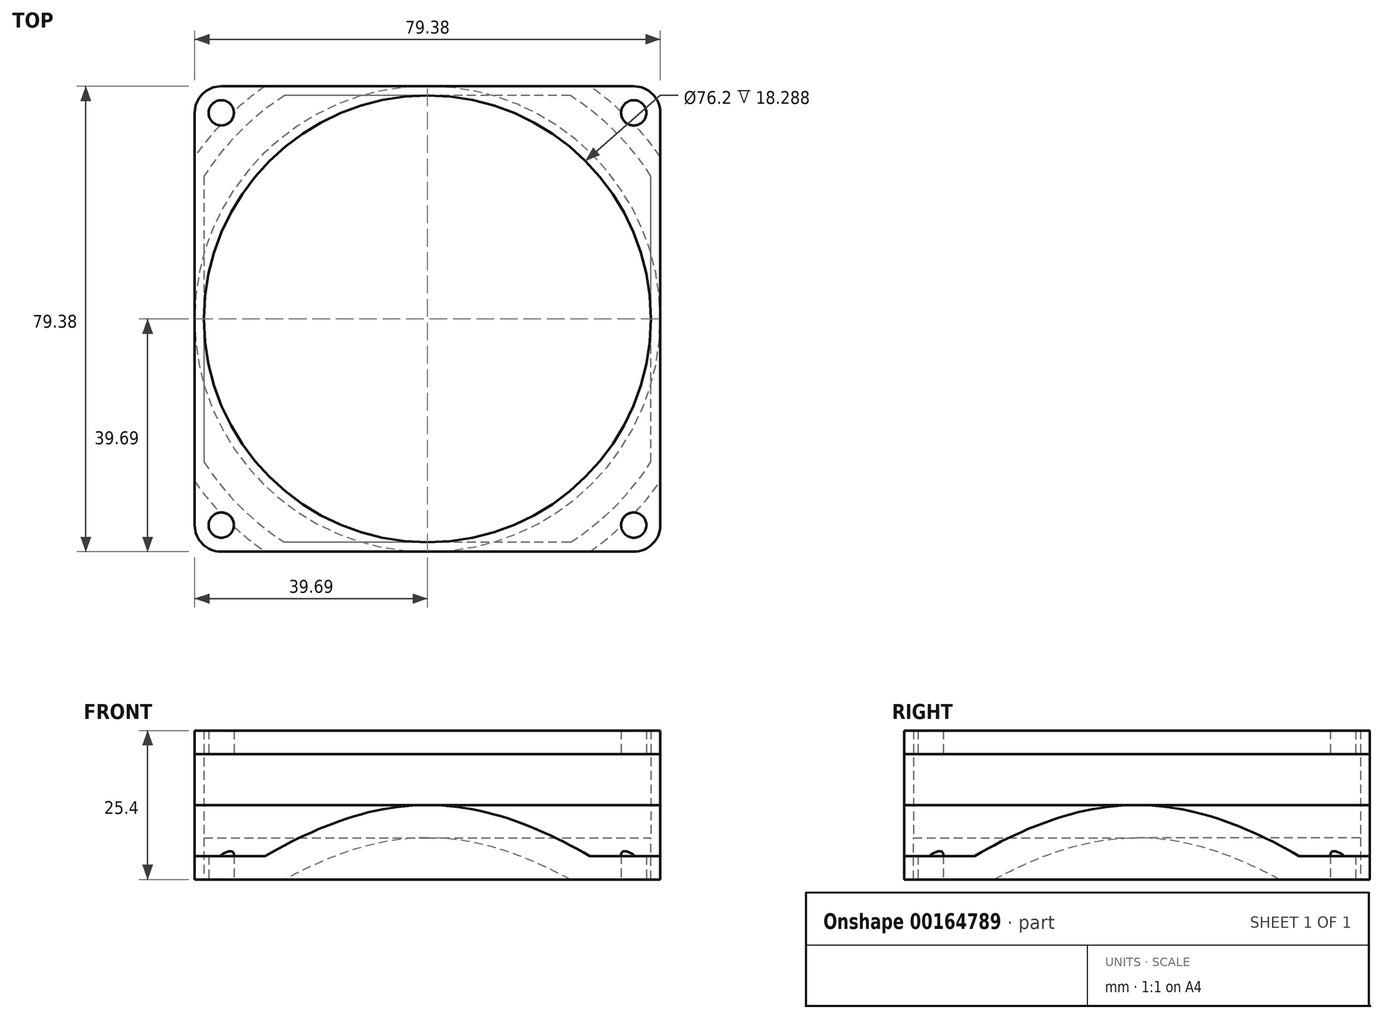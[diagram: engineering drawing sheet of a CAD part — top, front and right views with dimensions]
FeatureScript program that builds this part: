
annotation { "Feature Type Name" : "Feature", "Feature Type Description" : "" }
export const myFeature = defineFeature(function(context is Context, id is Id, definition is map)
    precondition{}
    {
        {
            var Q0;
            Q0=qCreatedBy(makeId("Top.planeOp"),FACE);
            var sketch = newSketch(context, id + "F0", { "sketchPlane" : qUnion([Q0])});
            skLineSegment(sketch, "E0.bottom", {"start": v(39.69, 39.69) * mm, "end": v(-39.69, 39.69) * mm});
            skLineSegment(sketch, "E0.top", {"start": v(39.69, -39.69) * mm, "end": v(-39.69, -39.69) * mm});
            skLineSegment(sketch, "E0.left", {"start": v(39.69, 39.69) * mm, "end": v(39.69, -39.69) * mm});
            skLineSegment(sketch, "E0.right", {"start": v(-39.69, 39.69) * mm, "end": v(-39.69, -39.69) * mm});
            skPoint(sketch, "E0.middle", {"position": v(0, 0) * mm});
            skCircle(sketch, "E1", {"center": v(0, 0) * mm, "radius": 38.1 * mm});
            skLineSegment(sketch, "E2", {"start": v(35.15, 39.69) * mm, "end": v(35.15, 35.15) * mm, "construction": true});
            skLineSegment(sketch, "E3", {"start": v(35.15, 35.15) * mm, "end": v(39.69, 35.15) * mm, "construction": true});
            skLineSegment(sketch, "E4.bottom", {"start": v(35.15, 35.15) * mm, "end": v(-35.15, 35.15) * mm, "construction": true});
            skLineSegment(sketch, "E4.top", {"start": v(35.15, -35.15) * mm, "end": v(-35.15, -35.15) * mm, "construction": true});
            skLineSegment(sketch, "E4.left", {"start": v(35.15, 35.15) * mm, "end": v(35.15, -35.15) * mm, "construction": true});
            skLineSegment(sketch, "E4.right", {"start": v(-35.15, 35.15) * mm, "end": v(-35.15, -35.15) * mm, "construction": true});
            skCircle(sketch, "E5", {"center": v(35.15, 35.15) * mm, "radius": 2.15 * mm});
            skCircle(sketch, "E6", {"center": v(-35.15, 35.15) * mm, "radius": 2.15 * mm});
            skCircle(sketch, "E7", {"center": v(-35.15, -35.15) * mm, "radius": 2.15 * mm});
            skCircle(sketch, "E8", {"center": v(35.15, -35.15) * mm, "radius": 2.15 * mm});
            skSolve(sketch);
        }
        {
            var Q0;
            Q0=qSketchRegion(id+"F0",true);
            extrude(context, id + "F1", {"entities" : qUnion([Q0]), "depth" : 25.4 * mm});
        }
        {
            var Q0;
            Q0=makeQuery(id+"F1.opExtrude","SWEPT_EDGE",EDGE,{"disambiguationData":[OSD([sQuery(id+"F0.wireOp",EDGE,"E0.bottom"),sQuery(id+"F0.wireOp",EDGE,"E0.left")])]});
            var Q1;
            Q1=makeQuery(id+"F1.opExtrude","SWEPT_EDGE",EDGE,{"disambiguationData":[OSD([sQuery(id+"F0.wireOp",EDGE,"E0.top"),sQuery(id+"F0.wireOp",EDGE,"E0.right")])]});
            var Q2;
            Q2=makeQuery(id+"F1.opExtrude","SWEPT_EDGE",EDGE,{"disambiguationData":[OSD([sQuery(id+"F0.wireOp",EDGE,"E0.top"),sQuery(id+"F0.wireOp",EDGE,"E0.left")])]});
            var Q3;
            Q3=makeQuery(id+"F1.opExtrude","SWEPT_EDGE",EDGE,{"disambiguationData":[OSD([sQuery(id+"F0.wireOp",EDGE,"E0.bottom"),sQuery(id+"F0.wireOp",EDGE,"E0.right")])]});
            fillet(context, id + "F2", {"entities" : qUnion([Q0, Q1, Q2, Q3]), "radius" : 4.53 * mm, "tangentPropagation" : true, "allowEdgeOverflow" : false});
        }
        {
            var Q0;
            Q0=qCreatedBy(makeId("Right.planeOp"),FACE);
            var sketch = newSketch(context, id + "F3", { "sketchPlane" : qUnion([Q0])});
            skLineSegment(sketch, "E9.bottom", {"start": v(39.69, 21.4) * mm, "end": v(65.09, 21.4) * mm});
            skLineSegment(sketch, "E9.top", {"start": v(39.69, 4) * mm, "end": v(65.09, 4) * mm});
            skLineSegment(sketch, "E9.left", {"start": v(39.69, 21.4) * mm, "end": v(39.69, 4) * mm});
            skLineSegment(sketch, "E9.right", {"start": v(65.09, 21.4) * mm, "end": v(65.09, 4) * mm});
            skLineSegment(sketch, "E10", {"start": v(39.69, 21.4) * mm, "end": v(39.69, 25.4) * mm, "construction": true});
            skLineSegment(sketch, "E11", {"start": v(39.69, 4) * mm, "end": v(39.69, 0) * mm, "construction": true});
            skSolve(sketch);
        }
        {
            var Q0;
            Q0=qSketchRegion(id+"F3",true);
            var Q1;
            Q1=makeQuery(id+"F1.opExtrude","SWEPT_FACE",FACE,{"disambiguationData":[OSD([sQuery(id+"F0.wireOp",EDGE,"E1")])]});
            revolve(context, id + "F4", {"operationType" : NewBodyOperationType.REMOVE, "entities" : qUnion([Q0]), "axis" : qUnion([Q1]), "revolveType" : RevolveType.FULL, "oppositeDirection" : true});
        }
        {
            var Q0;
            {var subQ0=sQuery(id+"F3.wireOp",EDGE,"E9.top");var subQ1=sQuery(id+"F3.wireOp",EDGE,"E9.left");Q0=makeQuery(id+"F4.boolean.opBoolean","COPY",EDGE,{"disambiguationData":[TD([makeQuery(id+"F1.opExtrude","SWEPT_FACE",FACE,{"disambiguationData":[OSD([sQuery(id+"F0.wireOp",EDGE,"E0.bottom")])]}),makeQuery(id+"F1.opExtrude","SWEPT_FACE",FACE,{"disambiguationData":[OSD([sQuery(id+"F0.wireOp",EDGE,"E0.left")])]}),makeQuery(id+"F4.opRevolve","SWEPT_FACE",FACE,{"disambiguationData":[OSD([subQ0])]}),makeQuery(id+"F4.opRevolve","SWEPT_FACE",FACE,{"disambiguationData":[OSD([subQ1])]})])],"derivedFrom":makeQuery(id+"F4.opRevolve","SWEPT_EDGE",EDGE,{"disambiguationData":[OSD([subQ0,subQ1])]})});}
            chamfer(context, id + "F5", {"entities" : qUnion([Q0]), "width" : 8.7 * mm, "tangentPropagation" : true});
        }
        {
            var Q0;
            Q0=makeQuery(id+"F1.opExtrude","CAP_EDGE",EDGE,{"disambiguationData":[OSD([sQuery(id+"F0.wireOp",EDGE,"E1")])],"isStart":true});
            chamfer(context, id + "F6", {"entities" : qUnion([Q0]), "width" : 7.11 * mm, "tangentPropagation" : true});
        }
        {
            var Q0;
            Q0=makeQuery(id+"F6.opChamfer","SPLIT",FACE,{"disambiguationData":[OD(0.0)],"derivedFrom":makeQuery(id+"F1.opExtrude","CAP_FACE",FACE,{"disambiguationData":[OSD([sQuery(id+"F0.wireOp",EDGE,"E0.bottom"),sQuery(id+"F0.wireOp",EDGE,"E0.top"),sQuery(id+"F0.wireOp",EDGE,"E0.left"),sQuery(id+"F0.wireOp",EDGE,"E0.right"),sQuery(id+"F0.wireOp",EDGE,"E1"),sQuery(id+"F0.wireOp",EDGE,"E5"),sQuery(id+"F0.wireOp",EDGE,"E6"),sQuery(id+"F0.wireOp",EDGE,"E7"),sQuery(id+"F0.wireOp",EDGE,"E8")])],"isStart":true})});
            var sketch = newSketch(context, id + "F7", { "sketchPlane" : qUnion([Q0])});
            skLineSegment(sketch, "E12.bottom", {"start": v(24.34, -39.69) * mm, "end": v(-24.34, -39.69) * mm});
            skLineSegment(sketch, "E12.top", {"start": v(24.34, -38.1) * mm, "end": v(-24.34, -38.1) * mm});
            skLineSegment(sketch, "E12.left", {"start": v(24.34, -39.69) * mm, "end": v(24.34, -38.1) * mm});
            skLineSegment(sketch, "E12.right", {"start": v(-24.34, -39.69) * mm, "end": v(-24.34, -38.1) * mm});
            skLineSegment(sketch, "E13.bottom", {"start": v(38.1, 24.34) * mm, "end": v(39.69, 24.34) * mm});
            skLineSegment(sketch, "E13.top", {"start": v(38.1, -24.34) * mm, "end": v(39.69, -24.34) * mm});
            skLineSegment(sketch, "E13.left", {"start": v(38.1, 24.34) * mm, "end": v(38.1, -24.34) * mm});
            skLineSegment(sketch, "E13.right", {"start": v(39.69, 24.34) * mm, "end": v(39.69, -24.34) * mm});
            skLineSegment(sketch, "E14.bottom", {"start": v(-38.1, -24.34) * mm, "end": v(-39.69, -24.34) * mm});
            skLineSegment(sketch, "E14.top", {"start": v(-38.1, 24.34) * mm, "end": v(-39.69, 24.34) * mm});
            skLineSegment(sketch, "E14.left", {"start": v(-38.1, -24.34) * mm, "end": v(-38.1, 24.34) * mm});
            skLineSegment(sketch, "E14.right", {"start": v(-39.69, -24.34) * mm, "end": v(-39.69, 24.34) * mm});
            skLineSegment(sketch, "E15.bottom", {"start": v(24.34, 39.69) * mm, "end": v(-24.34, 39.69) * mm});
            skLineSegment(sketch, "E15.top", {"start": v(24.34, 38.1) * mm, "end": v(-24.34, 38.1) * mm});
            skLineSegment(sketch, "E15.left", {"start": v(24.34, 39.69) * mm, "end": v(24.34, 38.1) * mm});
            skLineSegment(sketch, "E15.right", {"start": v(-24.34, 39.69) * mm, "end": v(-24.34, 38.1) * mm});
            skLineSegment(sketch, "E16", {"start": v(0, -38.1) * mm, "end": v(0, 38.1) * mm, "construction": true});
            skLineSegment(sketch, "E17", {"start": v(38.1, 0) * mm, "end": v(-38.1, 0) * mm, "construction": true});
            skSolve(sketch);
        }
        {
            var Q0;
            Q0=qSketchRegion(id+"F7",true);
            var Q1;
            {var subQ0=sQuery(id+"F3.wireOp",EDGE,"E9.top");var subQ1=sQuery(id+"F3.wireOp",EDGE,"E9.left");Q1=makeQuery(id+"F5.opChamfer","BLEND_FACE",FACE,{"disambiguationData":[OSD([subQ0,subQ1]),TDD([makeQuery(id+"F4.boolean.opBoolean","COPY",EDGE,{"disambiguationData":[TD([makeQuery(id+"F1.opExtrude","SWEPT_FACE",FACE,{"disambiguationData":[OSD([sQuery(id+"F0.wireOp",EDGE,"E0.top")])]}),makeQuery(id+"F1.opExtrude","SWEPT_FACE",FACE,{"disambiguationData":[OSD([sQuery(id+"F0.wireOp",EDGE,"E0.left")])]}),makeQuery(id+"F4.opRevolve","SWEPT_FACE",FACE,{"disambiguationData":[OSD([subQ0])]}),makeQuery(id+"F4.opRevolve","SWEPT_FACE",FACE,{"disambiguationData":[OSD([subQ1])]})])],"derivedFrom":makeQuery(id+"F4.opRevolve","SWEPT_EDGE",EDGE,{"disambiguationData":[OSD([subQ0,subQ1])]})})])]});}
            extrude(context, id + "F8", {"entities" : qUnion([Q0]), "operationType" : NewBodyOperationType.ADD, "endBound" : BoundingType.UP_TO_SURFACE, "oppositeDirection" : true, "endBoundEntityFace" : qUnion([Q1]), "depth" : 25.4 * mm});
        }
    });
